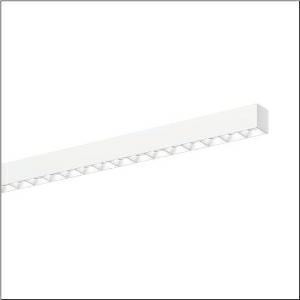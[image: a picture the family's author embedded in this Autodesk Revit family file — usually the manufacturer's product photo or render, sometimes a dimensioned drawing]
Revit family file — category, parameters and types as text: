
# Revit family: silica_r__21_51mx26db35wb_1250
name_source: partatom
category: Lighting Fixtures
units: mm (PartAtom-declared; Revit-internal decimal feet)

## family parameters
Cut with Voids When Loaded = No
Host = Face
Light Source = No
Part Type = Normal
Room Calculation Point = No
Round Connector Dimension = Use Diameter
Shared = No

## types (1)
- --- (1 x LED, 5400 lm, 31.4 W, 3000K)
    Apparent Load = 31 VA
    CIE Flux Codes = 83 98 100 100 100
    Color Rendering = 80
    Color Temperature = 3000K
    Default Elevation = 1800 mm
    Description = Silica® 21, office luminaire, primary light control with darklight reflector, of PMMA, white, CAT 2 (L<= 3000cd/m²), light emission: direct distribution, primary light characteristic: symmetric, installation type: surface-mounted, LED, rated luminous flux: 5.400lm, luminous efficacy: 172lm/W, light colour: 830, colour temperature: 3000K, control gear: DALI 2, with terminal, 3+2-pole, max. 2.5mm², mains connection: 220..240V, AC, 50/60Hz, rated input power: 31.4W, luminaire housing, of aluminium, traffic white (RAL 9016), length: 1.504mm, width: 53mm, height: 53mm, protection rating (complete): IP20, insulation class (complete): insulation class I (protective earthing), certification: CE, permissible operating ambient temperature: 0..+35°C, standard: EN 50419, packaging unit: 1 piece
    Height = 53 mm
    Lamp = 1 x LED
    Lamp Light Flux = 5400 lm
    Lamp Power = 31.4 W
    Lamp count = 1
    Length = 1504 mm
    Luminous efficacy = 172 lm/W
    Manufacturer = Siteco
    ModVariant = No
    Model = 51MX26DB35WB
    Mounting Place = Ceiling
    Mounting Type = Surface mounted
    Number of Poles = 1
    OnlyDefault = Yes
    Power Factor = 1
    Product Name = Silica® 21
    Product group = office luminaire | ceiling mounted
    ProductGroupID = 301
    Protection Class = Protection class I
    Protection Degree = IP 20
    RLX_Detail_Level = 1
    RLX_Emergency_Light_Flux = 0 lm
    RLX_Emergency_Type = 0
    RLX_Emergency_Type_DB = No
    RlxData = <blob elided: 42333 chars, md5=79d925f2>
    Socket = socket
    Standby Power = 0 W
    System Light Flux = 5400 lm
    System Power = 31 W
    Type Comments = factory setting: luminous flux: 100 % | dim-lin: 254 | 360 mA
    Type Image = l_1335934.jpg
    URL = http://relux.com
    VarID = @adj_121648
    Voltage = 0 V
    Weight = 0.00 kg
    Width = 53 mm

## geometry (parser evidence)
native form markers: Blend x4, Sweep x9
no freeform markers — native parametric forms only
